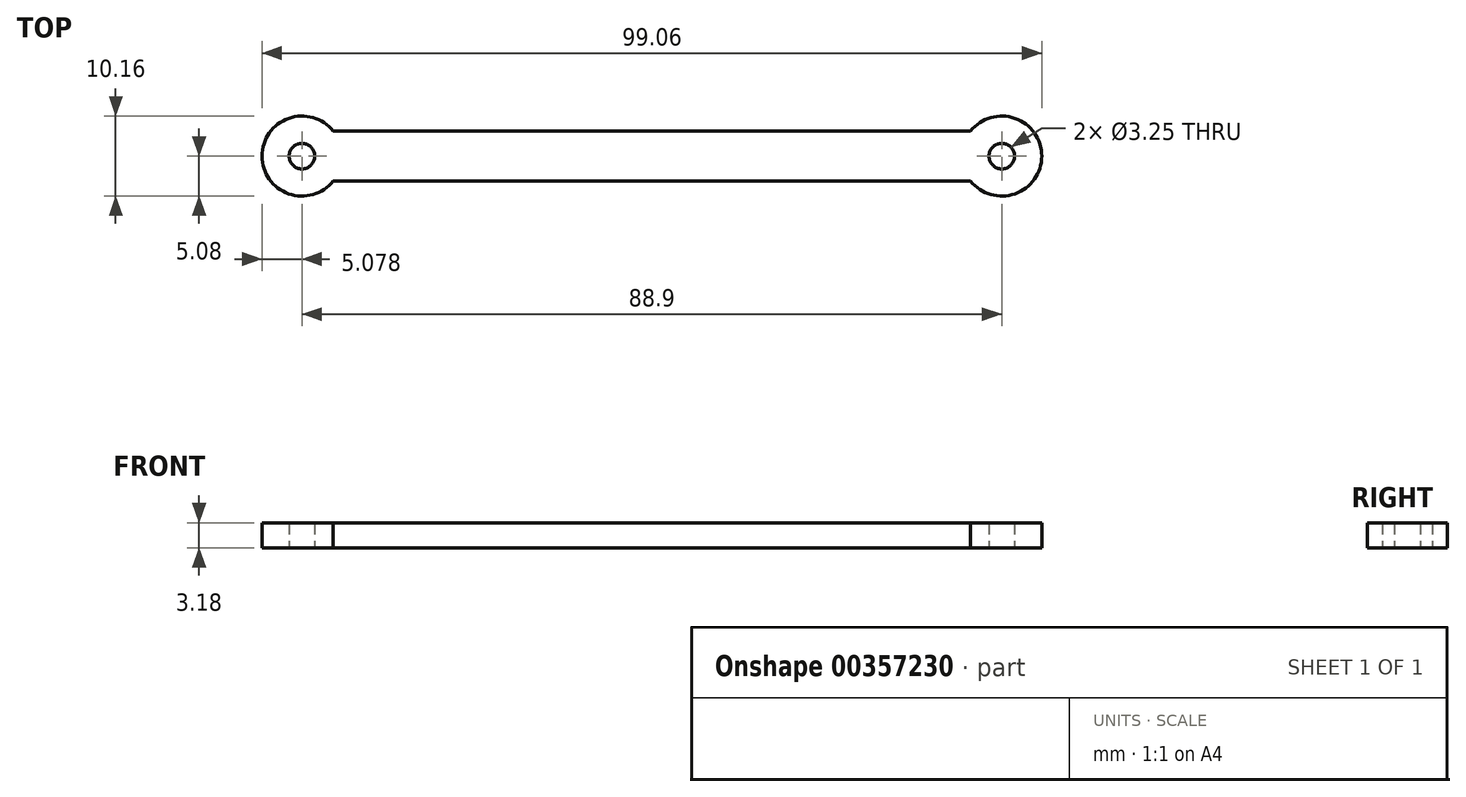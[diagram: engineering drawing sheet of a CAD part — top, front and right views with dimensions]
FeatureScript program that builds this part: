
annotation { "Feature Type Name" : "Feature", "Feature Type Description" : "" }
export const myFeature = defineFeature(function(context is Context, id is Id, definition is map)
    precondition{}
    {
        {
            var Q0;
            Q0=qCreatedBy(makeId("Top.planeOp"),FACE);
            var sketch = newSketch(context, id + "F0", { "sketchPlane" : qUnion([Q0])});
            skLineSegment(sketch, "E0.bottom", {"start": v(-46.32, -0.43) * mm, "end": v(42.58, -0.43) * mm});
            skLineSegment(sketch, "E0.top", {"start": v(-46.32, -6.78) * mm, "end": v(42.58, -6.78) * mm});
            skLineSegment(sketch, "E0.left", {"start": v(-46.32, -0.43) * mm, "end": v(-46.32, -6.78) * mm});
            skLineSegment(sketch, "E0.right", {"start": v(42.58, -0.43) * mm, "end": v(42.58, -6.78) * mm});
            skCircle(sketch, "E1", {"center": v(-46.32, -3.6) * mm, "radius": 5.08 * mm});
            skCircle(sketch, "E2", {"center": v(42.58, -3.6) * mm, "radius": 5.08 * mm});
            skSolve(sketch);
        }
        {
            var Q0;
            {var subQ0=sQuery(id+"F0.wireOp",EDGE,"E1");var subQ1=sQuery(id+"F0.wireOp",EDGE,"E0.bottom");var subQ2=makeQuery(id+"F0.imprint","INTERSECT",VERTEX,{"derivedFrom":[subQ1,subQ0]});Q0=makeQuery(id+"F0.imprint","IMPRINT",FACE,{"disambiguationData":[TD([[makeQuery(id+"F0.imprint","IMPRINT",EDGE,{"disambiguationData":[TD([[subQ2,-1.0]])],"derivedFrom":subQ1}),-1.0]])]});}
            var Q1;
            {var subQ0=sQuery(id+"F0.wireOp",EDGE,"E0.right");Q1=makeQuery(id+"F0.imprint","IMPRINT",FACE,{"disambiguationData":[TD([[makeQuery(id+"F0.imprint","IMPRINT",EDGE,{"derivedFrom":subQ0}),1.0]])]});}
            var Q2;
            {var subQ0=sQuery(id+"F0.wireOp",EDGE,"E0.right");Q2=makeQuery(id+"F0.imprint","IMPRINT",FACE,{"disambiguationData":[TD([[makeQuery(id+"F0.imprint","IMPRINT",EDGE,{"derivedFrom":subQ0}),-1.0]])]});}
            var Q3;
            {var subQ0=sQuery(id+"F0.wireOp",EDGE,"E0.left");Q3=makeQuery(id+"F0.imprint","IMPRINT",FACE,{"disambiguationData":[TD([[makeQuery(id+"F0.imprint","IMPRINT",EDGE,{"derivedFrom":subQ0}),1.0]])]});}
            var Q4;
            {var subQ0=sQuery(id+"F0.wireOp",EDGE,"E0.left");Q4=makeQuery(id+"F0.imprint","IMPRINT",FACE,{"disambiguationData":[TD([[makeQuery(id+"F0.imprint","IMPRINT",EDGE,{"derivedFrom":subQ0}),-1.0]])]});}
            extrude(context, id + "F1", {"entities" : qUnion([Q0, Q1, Q2, Q3, Q4]), "depth" : 3.17 * mm});
        }
        {
            var Q0;
            Q0=makeQuery(id+"F1.opExtrude","CAP_FACE",FACE,{"disambiguationData":[OSD([sQuery(id+"F0.wireOp",EDGE,"E0.bottom"),sQuery(id+"F0.wireOp",EDGE,"E0.top"),sQuery(id+"F0.wireOp",EDGE,"E1"),sQuery(id+"F0.wireOp",EDGE,"E2")])],"isStart":true});
            var sketch = newSketch(context, id + "F2", { "sketchPlane" : qUnion([Q0])});
            skPoint(sketch, "E3", {"position": v(-46.32, 3.6) * mm});
            skPoint(sketch, "E4", {"position": v(42.58, 3.6) * mm});
            skSolve(sketch);
        }
        {
            var Q0;
            Q0=sQuery(id+"F2.wireOp",VERTEX,"E3");
            var Q1;
            Q1=sQuery(id+"F2.wireOp",VERTEX,"E4");
            var Q2;
            Q2=makeQuery(id+"F1.opExtrude","SWEPT_BODY",BODY,{"disambiguationData":[OSD([sQuery(id+"F0.wireOp",EDGE,"E0.bottom"),sQuery(id+"F0.wireOp",EDGE,"E0.top"),sQuery(id+"F0.wireOp",EDGE,"E1"),sQuery(id+"F0.wireOp",EDGE,"E2")])]});
            hole(context, id + "F3", {"style" : HoleStyle.SIMPLE, "endStyle" : HoleEndStyle.THROUGH, "holeDiameter" : 3.25 * mm, "isTappedThrough" : true, "tappedDepth" : 12.7 * mm, "tapClearance" : 3, "locations" : qUnion([Q0, Q1]), "scope" : qUnion([Q2])});
        }
    });
